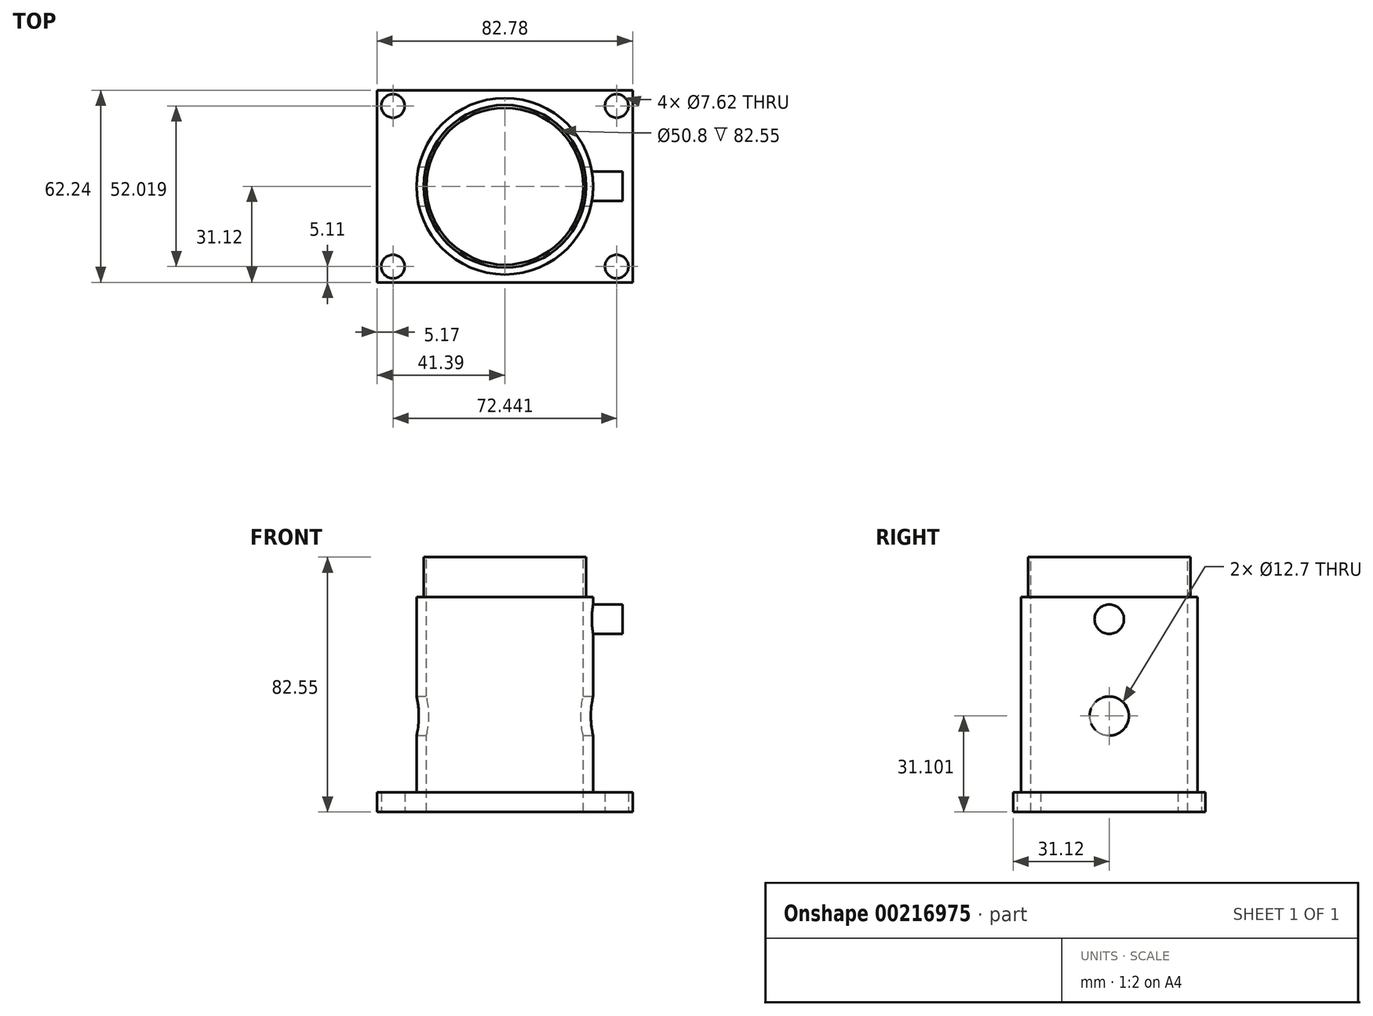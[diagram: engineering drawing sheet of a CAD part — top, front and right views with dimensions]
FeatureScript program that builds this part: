
annotation { "Feature Type Name" : "Feature", "Feature Type Description" : "" }
export const myFeature = defineFeature(function(context is Context, id is Id, definition is map)
    precondition{}
    {
        {
            var Q0;
            Q0=qCreatedBy(makeId("Top.planeOp"),FACE);
            var sketch = newSketch(context, id + "F0", { "sketchPlane" : qUnion([Q0])});
            skLineSegment(sketch, "E0.bottom", {"start": v(-315.57, 58.74) * mm, "end": v(-388, 58.74) * mm});
            skLineSegment(sketch, "E0.right", {"start": v(-388, 58.74) * mm, "end": v(-388, 110.76) * mm});
            skPoint(sketch, "E1.middle", {"position": v(0, 0) * mm});
            skCircle(sketch, "E2", {"center": v(-36.22, -26) * mm, "radius": 3.81 * mm});
            skCircle(sketch, "E3", {"center": v(-36.22, 26) * mm, "radius": 3.81 * mm});
            skCircle(sketch, "E4", {"center": v(36.22, 26) * mm, "radius": 3.81 * mm});
            skCircle(sketch, "E5", {"center": v(36.22, -26) * mm, "radius": 3.81 * mm});
            skLineSegment(sketch, "E6.bottom", {"start": v(-41.39, -31.12) * mm, "end": v(41.39, -31.12) * mm});
            skLineSegment(sketch, "E6.top", {"start": v(-41.39, 31.12) * mm, "end": v(41.39, 31.12) * mm});
            skLineSegment(sketch, "E6.left", {"start": v(-41.39, -31.12) * mm, "end": v(-41.39, 31.12) * mm});
            skLineSegment(sketch, "E6.right", {"start": v(41.39, -31.12) * mm, "end": v(41.39, 31.12) * mm});
            skSolve(sketch);
        }
        {
            var Q0;
            Q0=makeQuery(id+"F0.imprint","IMPRINT",FACE,{"disambiguationData":[TD([[makeQuery(id+"F0.imprint","IMPRINT",EDGE,{"derivedFrom":sQuery(id+"F0.wireOp",EDGE,"E2")}),-1.0]])]});
            extrude(context, id + "F1", {"entities" : qUnion([Q0]), "depth" : 6.35 * mm});
        }
        {
            var Q0;
            Q0=makeQuery(id+"F1.opExtrude","CAP_FACE",FACE,{"disambiguationData":[OSD([sQuery(id+"F0.wireOp",EDGE,"E2"),sQuery(id+"F0.wireOp",EDGE,"E3"),sQuery(id+"F0.wireOp",EDGE,"E4"),sQuery(id+"F0.wireOp",EDGE,"E5"),sQuery(id+"F0.wireOp",EDGE,"E6.bottom"),sQuery(id+"F0.wireOp",EDGE,"E6.top"),sQuery(id+"F0.wireOp",EDGE,"E6.left"),sQuery(id+"F0.wireOp",EDGE,"E6.right")])],"isStart":false});
            var sketch = newSketch(context, id + "F2", { "sketchPlane" : qUnion([Q0])});
            skCircle(sketch, "E7", {"center": v(0, 0) * mm, "radius": 28.58 * mm});
            skSolve(sketch);
        }
        {
            var Q0;
            Q0=makeQuery(id+"F2.imprint","IMPRINT",FACE,{"disambiguationData":[TD([[makeQuery(id+"F2.imprint","IMPRINT",EDGE,{"derivedFrom":sQuery(id+"F2.wireOp",EDGE,"E7")}),1.0]])]});
            extrude(context, id + "F3", {"entities" : qUnion([Q0]), "operationType" : NewBodyOperationType.ADD, "depth" : 76.2 * mm});
        }
        {
            var Q0;
            Q0=qCreatedBy(makeId("Right.planeOp"),FACE);
            var sketch = newSketch(context, id + "F4", { "sketchPlane" : qUnion([Q0])});
            skCircle(sketch, "E8", {"center": v(0, 31.1) * mm, "radius": 6.35 * mm});
            skSolve(sketch);
        }
        {
            var Q0;
            Q0 = qSketchRegion(id + "F4", true);
            extrude(context, id + "F5", {"entities" : qUnion([Q0]), "operationType" : NewBodyOperationType.REMOVE, "oppositeDirection" : true, "depth" : 50.8 * mm, "hasSecondDirection" : true, "secondDirectionOppositeDirection" : false, "secondDirectionDepth" : 50.8 * mm});
        }
        {
            var Q0;
            Q0=qCreatedBy(makeId("Right.planeOp"),FACE);
            var sketch = newSketch(context, id + "F6", { "sketchPlane" : qUnion([Q0])});
            skCircle(sketch, "E9", {"center": v(0, 62.46) * mm, "radius": 4.76 * mm});
            skSolve(sketch);
        }
        {
            var Q0;
            Q0 = qSketchRegion(id + "F6", true);
            extrude(context, id + "F7", {"entities" : qUnion([Q0]), "operationType" : NewBodyOperationType.ADD, "depth" : 38.1 * mm});
        }
        {
            var Q0;
            Q0=makeQuery(id+"F3.opExtrude","CAP_FACE",FACE,{"disambiguationData":[OSD([sQuery(id+"F2.wireOp",EDGE,"E7")])],"isStart":false});
            var sketch = newSketch(context, id + "F8", { "sketchPlane" : qUnion([Q0])});
            skCircle(sketch, "E10", {"center": v(0, 0) * mm, "radius": 26.31 * mm});
            skCircle(sketch, "E11", {"center": v(0, 0) * mm, "radius": 25.4 * mm});
            skSolve(sketch);
        }
        {
            var Q0;
            Q0=makeQuery(id+"F8.imprint","IMPRINT",FACE,{"disambiguationData":[TD([[makeQuery(id+"F8.imprint","IMPRINT",EDGE,{"derivedFrom":sQuery(id+"F8.wireOp",EDGE,"E11")}),1.0]])]});
            extrude(context, id + "F9", {"entities" : qUnion([Q0]), "operationType" : NewBodyOperationType.REMOVE, "endBound" : BoundingType.THROUGH_ALL, "oppositeDirection" : true, "depth" : 25.4 * mm});
        }
        {
            var Q0;
            Q0=makeQuery(id+"F8.imprint","IMPRINT",FACE,{"disambiguationData":[TD([[makeQuery(id+"F8.imprint","IMPRINT",EDGE,{"derivedFrom":sQuery(id+"F8.wireOp",EDGE,"E10")}),-1.0]])]});
            extrude(context, id + "F10", {"entities" : qUnion([Q0]), "operationType" : NewBodyOperationType.REMOVE, "oppositeDirection" : true, "depth" : 12.95 * mm});
        }
    });
